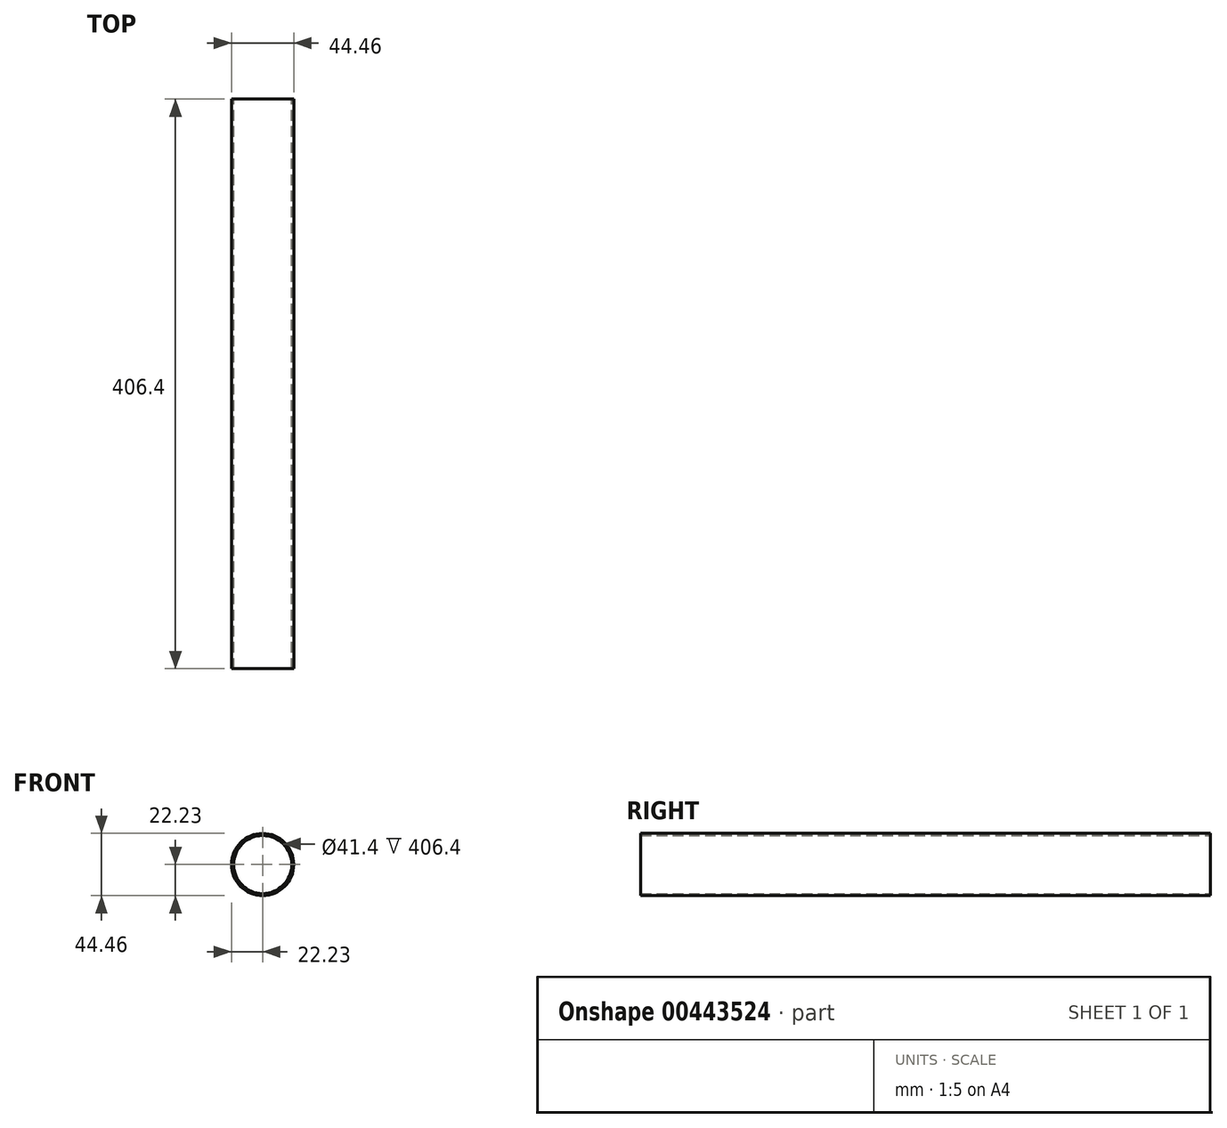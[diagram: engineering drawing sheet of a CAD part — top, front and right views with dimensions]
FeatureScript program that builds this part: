
annotation { "Feature Type Name" : "Feature", "Feature Type Description" : "" }
export const myFeature = defineFeature(function(context is Context, id is Id, definition is map)
    precondition{}
    {
        {
            var Q0;
            Q0=qCreatedBy(makeId("Front.planeOp"),FACE);
            var sketch = newSketch(context, id + "F0", { "sketchPlane" : qUnion([Q0])});
            skCircle(sketch, "E0", {"center": v(0, 0) * mm, "radius": 22.23 * mm});
            skCircle(sketch, "E1", {"center": v(0, 0) * mm, "radius": 20.7 * mm});
            skSolve(sketch);
        }
        {
            var Q0;
            Q0=makeQuery(id+"F0.imprint","IMPRINT",FACE,{"disambiguationData":[TD([[makeQuery(id+"F0.imprint","IMPRINT",EDGE,{"derivedFrom":sQuery(id+"F0.wireOp",EDGE,"E0")}),1.0]])]});
            extrude(context, id + "F1", {"entities" : qUnion([Q0]), "depth" : 406.4 * mm});
        }
    });
